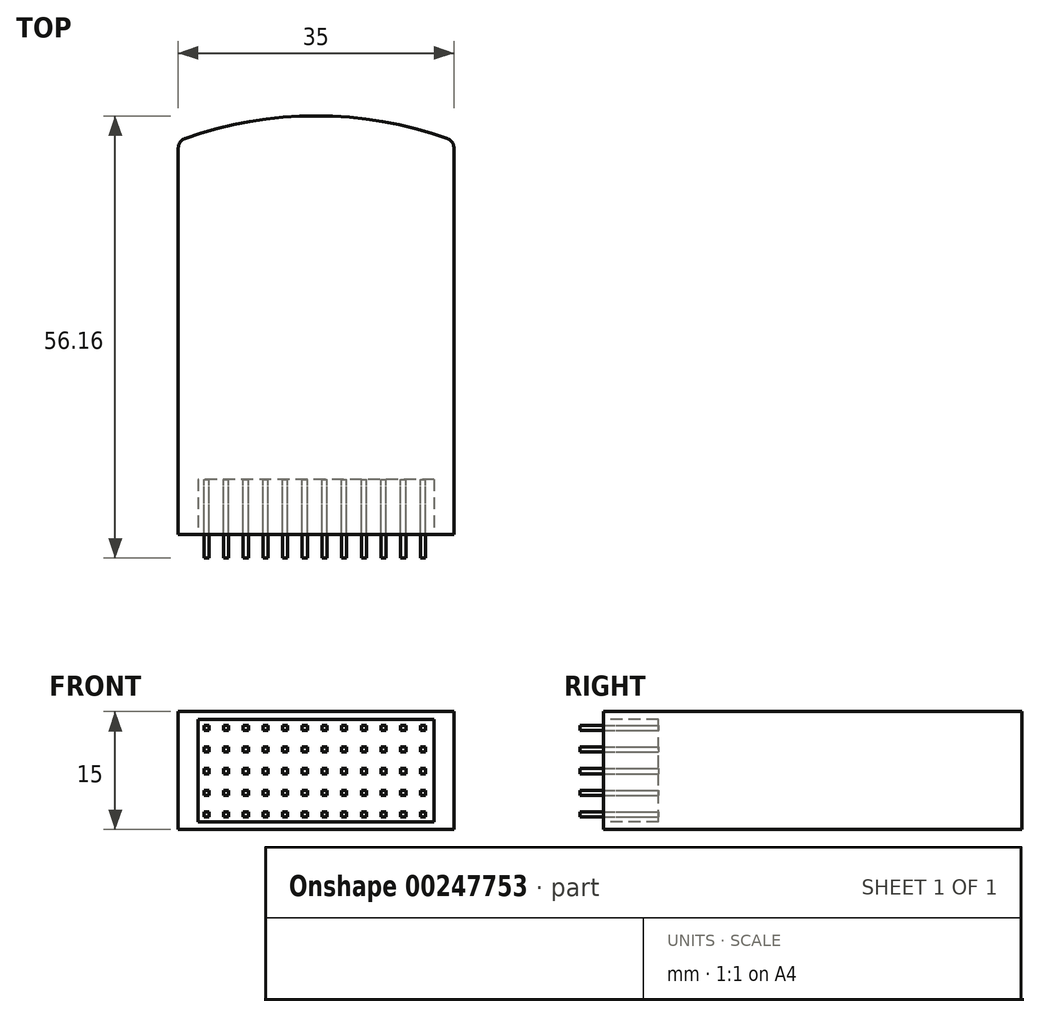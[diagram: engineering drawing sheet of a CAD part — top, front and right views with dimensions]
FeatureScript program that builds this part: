
annotation { "Feature Type Name" : "Feature", "Feature Type Description" : "" }
export const myFeature = defineFeature(function(context is Context, id is Id, definition is map)
    precondition{}
    {
        {
            var Q0;
            Q0=qCreatedBy(makeId("Top.planeOp"),FACE);
            var sketch = newSketch(context, id + "F0", { "sketchPlane" : qUnion([Q0])});
            skLineSegment(sketch, "E0.bottom", {"start": v(17.5, -25) * mm, "end": v(-17.5, -25) * mm});
            skLineSegment(sketch, "E0.top", {"start": v(17.5, 25) * mm, "end": v(-17.5, 25) * mm});
            skLineSegment(sketch, "E0.left", {"start": v(17.5, -25) * mm, "end": v(17.5, 25) * mm});
            skLineSegment(sketch, "E0.right", {"start": v(-17.5, -25) * mm, "end": v(-17.5, 25) * mm});
            skPoint(sketch, "E0.middle", {"position": v(0, 0) * mm});
            skPoint(sketch, "E1.startSnap0", {"position": v(0, 25) * mm});
            skArc(sketch, "E2", {"start": v(17.5, 25) * mm, "mid": v(0, 28.16) * mm, "end": v(-17.5, 25) * mm});
            skSolve(sketch);
        }
        {
            var Q0;
            Q0 = qSketchRegion(id + "F0", true);
            extrude(context, id + "F1", {"entities" : qUnion([Q0]), "depth" : 15 * mm, "symmetric" : true});
        }
        {
            var Q0;
            Q0=makeQuery(id+"F1.opExtrude","SWEPT_EDGE",EDGE,{"disambiguationData":[OSD([sQuery(id+"F0.wireOp",EDGE,"E0.top"),sQuery(id+"F0.wireOp",EDGE,"E0.left"),sQuery(id+"F0.wireOp",EDGE,"yyNhz9fe-Qt3a-qb7e-cI5q-L0wKWxCpfobD")])]});
            var Q1;
            Q1=makeQuery(id+"F1.opExtrude","SWEPT_EDGE",EDGE,{"disambiguationData":[OSD([sQuery(id+"F0.wireOp",EDGE,"E0.top"),sQuery(id+"F0.wireOp",EDGE,"E0.right"),sQuery(id+"F0.wireOp",EDGE,"NXXVwKCm-iX8Y-aLn6-gdMx-Pbhs1YLQSOhg")])]});
            fillet(context, id + "F2", {"entities" : qUnion([Q0, Q1]), "radius" : 1.25 * mm, "tangentPropagation" : true, "allowEdgeOverflow" : false});
        }
        {
            var Q0;
            Q0=makeQuery(id+"F1.opExtrude","SWEPT_FACE",FACE,{"disambiguationData":[OSD([sQuery(id+"F0.wireOp",EDGE,"E0.bottom")])]});
            var sketch = newSketch(context, id + "F3", { "sketchPlane" : qUnion([Q0])});
            skPoint(sketch, "E3.0", {"position": v(0, 0) * mm});
            skLineSegment(sketch, "E4.bottom", {"start": v(15, -6.5) * mm, "end": v(-15, -6.5) * mm});
            skLineSegment(sketch, "E4.top", {"start": v(15, 6.5) * mm, "end": v(-15, 6.5) * mm});
            skLineSegment(sketch, "E4.left", {"start": v(15, -6.5) * mm, "end": v(15, 6.5) * mm});
            skLineSegment(sketch, "E4.right", {"start": v(-15, -6.5) * mm, "end": v(-15, 6.5) * mm});
            skSolve(sketch);
        }
        {
            var Q0;
            Q0 = qSketchRegion(id + "F3", true);
            extrude(context, id + "F4", {"entities" : qUnion([Q0]), "operationType" : NewBodyOperationType.REMOVE, "oppositeDirection" : true, "depth" : 7 * mm});
        }
        {
            var Q0;
            Q0=makeQuery(id+"F4.boolean.opBoolean","COPY",FACE,{"derivedFrom":makeQuery(id+"F4.opExtrude","CAP_FACE",FACE,{"disambiguationData":[OSD([sQuery(id+"F3.wireOp",EDGE,"E4.bottom"),sQuery(id+"F3.wireOp",EDGE,"E4.top"),sQuery(id+"F3.wireOp",EDGE,"E4.left"),sQuery(id+"F3.wireOp",EDGE,"E4.right")])],"isStart":false})});
            var sketch = newSketch(context, id + "F5", { "sketchPlane" : qUnion([Q0])});
            skLineSegment(sketch, "E5.bottom", {"start": v(-14.25, 5.75) * mm, "end": v(-13.6, 5.75) * mm});
            skLineSegment(sketch, "E5.top", {"start": v(-14.25, 5.1) * mm, "end": v(-13.6, 5.1) * mm});
            skLineSegment(sketch, "E5.left", {"start": v(-14.25, 5.75) * mm, "end": v(-14.25, 5.1) * mm});
            skLineSegment(sketch, "E5.right", {"start": v(-13.6, 5.75) * mm, "end": v(-13.6, 5.1) * mm});
            skLineSegment(sketch, "E6.1.0.0", {"start": v(-11.75, 5.75) * mm, "end": v(-11.1, 5.75) * mm});
            skLineSegment(sketch, "E6.1.0.1", {"start": v(-11.75, 5.75) * mm, "end": v(-11.75, 5.1) * mm});
            skLineSegment(sketch, "E6.1.0.2", {"start": v(-11.75, 5.1) * mm, "end": v(-11.1, 5.1) * mm});
            skLineSegment(sketch, "E6.1.0.3", {"start": v(-11.1, 5.75) * mm, "end": v(-11.1, 5.1) * mm});
            skLineSegment(sketch, "E6.2.0.0", {"start": v(-9.25, 5.75) * mm, "end": v(-8.6, 5.75) * mm});
            skLineSegment(sketch, "E6.2.0.1", {"start": v(-9.25, 5.75) * mm, "end": v(-9.25, 5.1) * mm});
            skLineSegment(sketch, "E6.2.0.2", {"start": v(-9.25, 5.1) * mm, "end": v(-8.6, 5.1) * mm});
            skLineSegment(sketch, "E6.2.0.3", {"start": v(-8.6, 5.75) * mm, "end": v(-8.6, 5.1) * mm});
            skLineSegment(sketch, "E6.3.0.0", {"start": v(-6.75, 5.75) * mm, "end": v(-6.1, 5.75) * mm});
            skLineSegment(sketch, "E6.3.0.1", {"start": v(-6.75, 5.75) * mm, "end": v(-6.75, 5.1) * mm});
            skLineSegment(sketch, "E6.3.0.2", {"start": v(-6.75, 5.1) * mm, "end": v(-6.1, 5.1) * mm});
            skLineSegment(sketch, "E6.3.0.3", {"start": v(-6.1, 5.75) * mm, "end": v(-6.1, 5.1) * mm});
            skLineSegment(sketch, "E6.4.0.0", {"start": v(-4.25, 5.75) * mm, "end": v(-3.6, 5.75) * mm});
            skLineSegment(sketch, "E6.4.0.1", {"start": v(-4.25, 5.75) * mm, "end": v(-4.25, 5.1) * mm});
            skLineSegment(sketch, "E6.4.0.2", {"start": v(-4.25, 5.1) * mm, "end": v(-3.6, 5.1) * mm});
            skLineSegment(sketch, "E6.4.0.3", {"start": v(-3.6, 5.75) * mm, "end": v(-3.6, 5.1) * mm});
            skLineSegment(sketch, "E6.5.0.0", {"start": v(-1.75, 5.75) * mm, "end": v(-1.1, 5.75) * mm});
            skLineSegment(sketch, "E6.5.0.1", {"start": v(-1.75, 5.75) * mm, "end": v(-1.75, 5.1) * mm});
            skLineSegment(sketch, "E6.5.0.2", {"start": v(-1.75, 5.1) * mm, "end": v(-1.1, 5.1) * mm});
            skLineSegment(sketch, "E6.5.0.3", {"start": v(-1.1, 5.75) * mm, "end": v(-1.1, 5.1) * mm});
            skLineSegment(sketch, "E6.6.0.0", {"start": v(0.75, 5.75) * mm, "end": v(1.4, 5.75) * mm});
            skLineSegment(sketch, "E6.6.0.1", {"start": v(0.75, 5.75) * mm, "end": v(0.75, 5.1) * mm});
            skLineSegment(sketch, "E6.6.0.2", {"start": v(0.75, 5.1) * mm, "end": v(1.4, 5.1) * mm});
            skLineSegment(sketch, "E6.6.0.3", {"start": v(1.4, 5.75) * mm, "end": v(1.4, 5.1) * mm});
            skLineSegment(sketch, "E6.7.0.0", {"start": v(3.25, 5.75) * mm, "end": v(3.9, 5.75) * mm});
            skLineSegment(sketch, "E6.7.0.1", {"start": v(3.25, 5.75) * mm, "end": v(3.25, 5.1) * mm});
            skLineSegment(sketch, "E6.7.0.2", {"start": v(3.25, 5.1) * mm, "end": v(3.9, 5.1) * mm});
            skLineSegment(sketch, "E6.7.0.3", {"start": v(3.9, 5.75) * mm, "end": v(3.9, 5.1) * mm});
            skLineSegment(sketch, "E6.8.0.0", {"start": v(5.75, 5.75) * mm, "end": v(6.4, 5.75) * mm});
            skLineSegment(sketch, "E6.8.0.1", {"start": v(5.75, 5.75) * mm, "end": v(5.75, 5.1) * mm});
            skLineSegment(sketch, "E6.8.0.2", {"start": v(5.75, 5.1) * mm, "end": v(6.4, 5.1) * mm});
            skLineSegment(sketch, "E6.8.0.3", {"start": v(6.4, 5.75) * mm, "end": v(6.4, 5.1) * mm});
            skLineSegment(sketch, "E6.9.0.0", {"start": v(8.25, 5.75) * mm, "end": v(8.9, 5.75) * mm});
            skLineSegment(sketch, "E6.9.0.1", {"start": v(8.25, 5.75) * mm, "end": v(8.25, 5.1) * mm});
            skLineSegment(sketch, "E6.9.0.2", {"start": v(8.25, 5.1) * mm, "end": v(8.9, 5.1) * mm});
            skLineSegment(sketch, "E6.9.0.3", {"start": v(8.9, 5.75) * mm, "end": v(8.9, 5.1) * mm});
            skLineSegment(sketch, "E6.10.0.0", {"start": v(10.75, 5.75) * mm, "end": v(11.4, 5.75) * mm});
            skLineSegment(sketch, "E6.10.0.1", {"start": v(10.75, 5.75) * mm, "end": v(10.75, 5.1) * mm});
            skLineSegment(sketch, "E6.10.0.2", {"start": v(10.75, 5.1) * mm, "end": v(11.4, 5.1) * mm});
            skLineSegment(sketch, "E6.10.0.3", {"start": v(11.4, 5.75) * mm, "end": v(11.4, 5.1) * mm});
            skLineSegment(sketch, "E6.direction1", {"start": v(-14.25, 5.75) * mm, "end": v(-11.75, 5.75) * mm, "construction": true});
            skLineSegment(sketch, "E7.0.11.0", {"start": v(13.25, 5.75) * mm, "end": v(13.9, 5.75) * mm});
            skLineSegment(sketch, "E7.3.11.0", {"start": v(13.25, 5.75) * mm, "end": v(13.25, 5.1) * mm});
            skLineSegment(sketch, "E7.6.11.0", {"start": v(13.25, 5.1) * mm, "end": v(13.9, 5.1) * mm});
            skLineSegment(sketch, "E7.9.11.0", {"start": v(13.9, 5.75) * mm, "end": v(13.9, 5.1) * mm});
            skLineSegment(sketch, "E8.1.0.0", {"start": v(0.75, 3) * mm, "end": v(0.75, 2.35) * mm});
            skLineSegment(sketch, "E8.1.0.1", {"start": v(-6.75, 3) * mm, "end": v(-6.1, 3) * mm});
            skLineSegment(sketch, "E8.1.0.2", {"start": v(10.75, 3) * mm, "end": v(10.75, 2.35) * mm});
            skLineSegment(sketch, "E8.1.0.3", {"start": v(5.75, 2.35) * mm, "end": v(6.4, 2.35) * mm});
            skLineSegment(sketch, "E8.1.0.4", {"start": v(-4.25, 2.35) * mm, "end": v(-3.6, 2.35) * mm});
            skLineSegment(sketch, "E8.1.0.5", {"start": v(3.9, 3) * mm, "end": v(3.9, 2.35) * mm});
            skLineSegment(sketch, "E8.1.0.6", {"start": v(8.25, 2.35) * mm, "end": v(8.9, 2.35) * mm});
            skLineSegment(sketch, "E8.1.0.7", {"start": v(13.25, 2.35) * mm, "end": v(13.9, 2.35) * mm});
            skLineSegment(sketch, "E8.1.0.8", {"start": v(-1.75, 2.35) * mm, "end": v(-1.1, 2.35) * mm});
            skLineSegment(sketch, "E8.1.0.9", {"start": v(-8.6, 3) * mm, "end": v(-8.6, 2.35) * mm});
            skLineSegment(sketch, "E8.1.0.10", {"start": v(-9.25, 2.35) * mm, "end": v(-8.6, 2.35) * mm});
            skLineSegment(sketch, "E8.1.0.11", {"start": v(-9.25, 3) * mm, "end": v(-9.25, 2.35) * mm});
            skLineSegment(sketch, "E8.1.0.12", {"start": v(-9.25, 3) * mm, "end": v(-8.6, 3) * mm});
            skLineSegment(sketch, "E8.1.0.13", {"start": v(-11.1, 3) * mm, "end": v(-11.1, 2.35) * mm});
            skLineSegment(sketch, "E8.1.0.14", {"start": v(-11.75, 2.35) * mm, "end": v(-11.1, 2.35) * mm});
            skLineSegment(sketch, "E8.1.0.15", {"start": v(-11.75, 3) * mm, "end": v(-11.75, 2.35) * mm});
            skLineSegment(sketch, "E8.1.0.16", {"start": v(-11.75, 3) * mm, "end": v(-11.1, 3) * mm});
            skLineSegment(sketch, "E8.1.0.17", {"start": v(-13.6, 3) * mm, "end": v(-13.6, 2.35) * mm});
            skLineSegment(sketch, "E8.1.0.18", {"start": v(-14.25, 3) * mm, "end": v(-14.25, 2.35) * mm});
            skLineSegment(sketch, "E8.1.0.19", {"start": v(-14.25, 2.35) * mm, "end": v(-13.6, 2.35) * mm});
            skLineSegment(sketch, "E8.1.0.20", {"start": v(-4.25, 3) * mm, "end": v(-4.25, 2.35) * mm});
            skLineSegment(sketch, "E8.1.0.21", {"start": v(-6.1, 3) * mm, "end": v(-6.1, 2.35) * mm});
            skLineSegment(sketch, "E8.1.0.22", {"start": v(8.25, 3) * mm, "end": v(8.25, 2.35) * mm});
            skLineSegment(sketch, "E8.1.0.23", {"start": v(3.25, 2.35) * mm, "end": v(3.9, 2.35) * mm});
            skLineSegment(sketch, "E8.1.0.24", {"start": v(13.25, 3) * mm, "end": v(13.25, 2.35) * mm});
            skLineSegment(sketch, "E8.1.0.25", {"start": v(-6.75, 2.35) * mm, "end": v(-6.1, 2.35) * mm});
            skLineSegment(sketch, "E8.1.0.26", {"start": v(-1.75, 3) * mm, "end": v(-1.75, 2.35) * mm});
            skLineSegment(sketch, "E8.1.0.27", {"start": v(-6.75, 3) * mm, "end": v(-6.75, 2.35) * mm});
            skLineSegment(sketch, "E8.1.0.28", {"start": v(0.75, 3) * mm, "end": v(1.4, 3) * mm});
            skLineSegment(sketch, "E8.1.0.29", {"start": v(10.75, 3) * mm, "end": v(11.4, 3) * mm});
            skLineSegment(sketch, "E8.1.0.30", {"start": v(3.25, 3) * mm, "end": v(3.9, 3) * mm});
            skLineSegment(sketch, "E8.1.0.31", {"start": v(-14.25, 3) * mm, "end": v(-11.75, 3) * mm, "construction": true});
            skLineSegment(sketch, "E8.1.0.32", {"start": v(5.75, 3) * mm, "end": v(5.75, 2.35) * mm});
            skLineSegment(sketch, "E8.1.0.33", {"start": v(-1.1, 3) * mm, "end": v(-1.1, 2.35) * mm});
            skLineSegment(sketch, "E8.1.0.34", {"start": v(8.9, 3) * mm, "end": v(8.9, 2.35) * mm});
            skLineSegment(sketch, "E8.1.0.35", {"start": v(8.25, 3) * mm, "end": v(8.9, 3) * mm});
            skLineSegment(sketch, "E8.1.0.36", {"start": v(3.25, 3) * mm, "end": v(3.25, 2.35) * mm});
            skLineSegment(sketch, "E8.1.0.37", {"start": v(13.25, 3) * mm, "end": v(13.9, 3) * mm});
            skLineSegment(sketch, "E8.1.0.38", {"start": v(-1.75, 3) * mm, "end": v(-1.1, 3) * mm});
            skLineSegment(sketch, "E8.1.0.39", {"start": v(1.4, 3) * mm, "end": v(1.4, 2.35) * mm});
            skLineSegment(sketch, "E8.1.0.40", {"start": v(11.4, 3) * mm, "end": v(11.4, 2.35) * mm});
            skLineSegment(sketch, "E8.1.0.41", {"start": v(5.75, 3) * mm, "end": v(6.4, 3) * mm});
            skLineSegment(sketch, "E8.1.0.42", {"start": v(13.9, 3) * mm, "end": v(13.9, 2.35) * mm});
            skLineSegment(sketch, "E8.1.0.43", {"start": v(-4.25, 3) * mm, "end": v(-3.6, 3) * mm});
            skLineSegment(sketch, "E8.1.0.44", {"start": v(6.4, 3) * mm, "end": v(6.4, 2.35) * mm});
            skLineSegment(sketch, "E8.1.0.45", {"start": v(-3.6, 3) * mm, "end": v(-3.6, 2.35) * mm});
            skLineSegment(sketch, "E8.1.0.46", {"start": v(0.75, 2.35) * mm, "end": v(1.4, 2.35) * mm});
            skLineSegment(sketch, "E8.1.0.47", {"start": v(10.75, 2.35) * mm, "end": v(11.4, 2.35) * mm});
            skLineSegment(sketch, "E8.1.0.48", {"start": v(-14.25, 3) * mm, "end": v(-13.6, 3) * mm});
            skLineSegment(sketch, "E8.2.0.0", {"start": v(0.75, 0.25) * mm, "end": v(0.75, -0.4) * mm});
            skLineSegment(sketch, "E8.2.0.1", {"start": v(-6.75, 0.25) * mm, "end": v(-6.1, 0.25) * mm});
            skLineSegment(sketch, "E8.2.0.2", {"start": v(10.75, 0.25) * mm, "end": v(10.75, -0.4) * mm});
            skLineSegment(sketch, "E8.2.0.3", {"start": v(5.75, -0.4) * mm, "end": v(6.4, -0.4) * mm});
            skLineSegment(sketch, "E8.2.0.4", {"start": v(-4.25, -0.4) * mm, "end": v(-3.6, -0.4) * mm});
            skLineSegment(sketch, "E8.2.0.5", {"start": v(3.9, 0.25) * mm, "end": v(3.9, -0.4) * mm});
            skLineSegment(sketch, "E8.2.0.6", {"start": v(8.25, -0.4) * mm, "end": v(8.9, -0.4) * mm});
            skLineSegment(sketch, "E8.2.0.7", {"start": v(13.25, -0.4) * mm, "end": v(13.9, -0.4) * mm});
            skLineSegment(sketch, "E8.2.0.8", {"start": v(-1.75, -0.4) * mm, "end": v(-1.1, -0.4) * mm});
            skLineSegment(sketch, "E8.2.0.9", {"start": v(-8.6, 0.25) * mm, "end": v(-8.6, -0.4) * mm});
            skLineSegment(sketch, "E8.2.0.10", {"start": v(-9.25, -0.4) * mm, "end": v(-8.6, -0.4) * mm});
            skLineSegment(sketch, "E8.2.0.11", {"start": v(-9.25, 0.25) * mm, "end": v(-9.25, -0.4) * mm});
            skLineSegment(sketch, "E8.2.0.12", {"start": v(-9.25, 0.25) * mm, "end": v(-8.6, 0.25) * mm});
            skLineSegment(sketch, "E8.2.0.13", {"start": v(-11.1, 0.25) * mm, "end": v(-11.1, -0.4) * mm});
            skLineSegment(sketch, "E8.2.0.14", {"start": v(-11.75, -0.4) * mm, "end": v(-11.1, -0.4) * mm});
            skLineSegment(sketch, "E8.2.0.15", {"start": v(-11.75, 0.25) * mm, "end": v(-11.75, -0.4) * mm});
            skLineSegment(sketch, "E8.2.0.16", {"start": v(-11.75, 0.25) * mm, "end": v(-11.1, 0.25) * mm});
            skLineSegment(sketch, "E8.2.0.17", {"start": v(-13.6, 0.25) * mm, "end": v(-13.6, -0.4) * mm});
            skLineSegment(sketch, "E8.2.0.18", {"start": v(-14.25, 0.25) * mm, "end": v(-14.25, -0.4) * mm});
            skLineSegment(sketch, "E8.2.0.19", {"start": v(-14.25, -0.4) * mm, "end": v(-13.6, -0.4) * mm});
            skLineSegment(sketch, "E8.2.0.20", {"start": v(-4.25, 0.25) * mm, "end": v(-4.25, -0.4) * mm});
            skLineSegment(sketch, "E8.2.0.21", {"start": v(-6.1, 0.25) * mm, "end": v(-6.1, -0.4) * mm});
            skLineSegment(sketch, "E8.2.0.22", {"start": v(8.25, 0.25) * mm, "end": v(8.25, -0.4) * mm});
            skLineSegment(sketch, "E8.2.0.23", {"start": v(3.25, -0.4) * mm, "end": v(3.9, -0.4) * mm});
            skLineSegment(sketch, "E8.2.0.24", {"start": v(13.25, 0.25) * mm, "end": v(13.25, -0.4) * mm});
            skLineSegment(sketch, "E8.2.0.25", {"start": v(-6.75, -0.4) * mm, "end": v(-6.1, -0.4) * mm});
            skLineSegment(sketch, "E8.2.0.26", {"start": v(-1.75, 0.25) * mm, "end": v(-1.75, -0.4) * mm});
            skLineSegment(sketch, "E8.2.0.27", {"start": v(-6.75, 0.25) * mm, "end": v(-6.75, -0.4) * mm});
            skLineSegment(sketch, "E8.2.0.28", {"start": v(0.75, 0.25) * mm, "end": v(1.4, 0.25) * mm});
            skLineSegment(sketch, "E8.2.0.29", {"start": v(10.75, 0.25) * mm, "end": v(11.4, 0.25) * mm});
            skLineSegment(sketch, "E8.2.0.30", {"start": v(3.25, 0.25) * mm, "end": v(3.9, 0.25) * mm});
            skLineSegment(sketch, "E8.2.0.31", {"start": v(-14.25, 0.25) * mm, "end": v(-11.75, 0.25) * mm, "construction": true});
            skLineSegment(sketch, "E8.2.0.32", {"start": v(5.75, 0.25) * mm, "end": v(5.75, -0.4) * mm});
            skLineSegment(sketch, "E8.2.0.33", {"start": v(-1.1, 0.25) * mm, "end": v(-1.1, -0.4) * mm});
            skLineSegment(sketch, "E8.2.0.34", {"start": v(8.9, 0.25) * mm, "end": v(8.9, -0.4) * mm});
            skLineSegment(sketch, "E8.2.0.35", {"start": v(8.25, 0.25) * mm, "end": v(8.9, 0.25) * mm});
            skLineSegment(sketch, "E8.2.0.36", {"start": v(3.25, 0.25) * mm, "end": v(3.25, -0.4) * mm});
            skLineSegment(sketch, "E8.2.0.37", {"start": v(13.25, 0.25) * mm, "end": v(13.9, 0.25) * mm});
            skLineSegment(sketch, "E8.2.0.38", {"start": v(-1.75, 0.25) * mm, "end": v(-1.1, 0.25) * mm});
            skLineSegment(sketch, "E8.2.0.39", {"start": v(1.4, 0.25) * mm, "end": v(1.4, -0.4) * mm});
            skLineSegment(sketch, "E8.2.0.40", {"start": v(11.4, 0.25) * mm, "end": v(11.4, -0.4) * mm});
            skLineSegment(sketch, "E8.2.0.41", {"start": v(5.75, 0.25) * mm, "end": v(6.4, 0.25) * mm});
            skLineSegment(sketch, "E8.2.0.42", {"start": v(13.9, 0.25) * mm, "end": v(13.9, -0.4) * mm});
            skLineSegment(sketch, "E8.2.0.43", {"start": v(-4.25, 0.25) * mm, "end": v(-3.6, 0.25) * mm});
            skLineSegment(sketch, "E8.2.0.44", {"start": v(6.4, 0.25) * mm, "end": v(6.4, -0.4) * mm});
            skLineSegment(sketch, "E8.2.0.45", {"start": v(-3.6, 0.25) * mm, "end": v(-3.6, -0.4) * mm});
            skLineSegment(sketch, "E8.2.0.46", {"start": v(0.75, -0.4) * mm, "end": v(1.4, -0.4) * mm});
            skLineSegment(sketch, "E8.2.0.47", {"start": v(10.75, -0.4) * mm, "end": v(11.4, -0.4) * mm});
            skLineSegment(sketch, "E8.2.0.48", {"start": v(-14.25, 0.25) * mm, "end": v(-13.6, 0.25) * mm});
            skLineSegment(sketch, "E8.3.0.0", {"start": v(0.75, -2.5) * mm, "end": v(0.75, -3.15) * mm});
            skLineSegment(sketch, "E8.3.0.1", {"start": v(-6.75, -2.5) * mm, "end": v(-6.1, -2.5) * mm});
            skLineSegment(sketch, "E8.3.0.2", {"start": v(10.75, -2.5) * mm, "end": v(10.75, -3.15) * mm});
            skLineSegment(sketch, "E8.3.0.3", {"start": v(5.75, -3.15) * mm, "end": v(6.4, -3.15) * mm});
            skLineSegment(sketch, "E8.3.0.4", {"start": v(-4.25, -3.15) * mm, "end": v(-3.6, -3.15) * mm});
            skLineSegment(sketch, "E8.3.0.5", {"start": v(3.9, -2.5) * mm, "end": v(3.9, -3.15) * mm});
            skLineSegment(sketch, "E8.3.0.6", {"start": v(8.25, -3.15) * mm, "end": v(8.9, -3.15) * mm});
            skLineSegment(sketch, "E8.3.0.7", {"start": v(13.25, -3.15) * mm, "end": v(13.9, -3.15) * mm});
            skLineSegment(sketch, "E8.3.0.8", {"start": v(-1.75, -3.15) * mm, "end": v(-1.1, -3.15) * mm});
            skLineSegment(sketch, "E8.3.0.9", {"start": v(-8.6, -2.5) * mm, "end": v(-8.6, -3.15) * mm});
            skLineSegment(sketch, "E8.3.0.10", {"start": v(-9.25, -3.15) * mm, "end": v(-8.6, -3.15) * mm});
            skLineSegment(sketch, "E8.3.0.11", {"start": v(-9.25, -2.5) * mm, "end": v(-9.25, -3.15) * mm});
            skLineSegment(sketch, "E8.3.0.12", {"start": v(-9.25, -2.5) * mm, "end": v(-8.6, -2.5) * mm});
            skLineSegment(sketch, "E8.3.0.13", {"start": v(-11.1, -2.5) * mm, "end": v(-11.1, -3.15) * mm});
            skLineSegment(sketch, "E8.3.0.14", {"start": v(-11.75, -3.15) * mm, "end": v(-11.1, -3.15) * mm});
            skLineSegment(sketch, "E8.3.0.15", {"start": v(-11.75, -2.5) * mm, "end": v(-11.75, -3.15) * mm});
            skLineSegment(sketch, "E8.3.0.16", {"start": v(-11.75, -2.5) * mm, "end": v(-11.1, -2.5) * mm});
            skLineSegment(sketch, "E8.3.0.17", {"start": v(-13.6, -2.5) * mm, "end": v(-13.6, -3.15) * mm});
            skLineSegment(sketch, "E8.3.0.18", {"start": v(-14.25, -2.5) * mm, "end": v(-14.25, -3.15) * mm});
            skLineSegment(sketch, "E8.3.0.19", {"start": v(-14.25, -3.15) * mm, "end": v(-13.6, -3.15) * mm});
            skLineSegment(sketch, "E8.3.0.20", {"start": v(-4.25, -2.5) * mm, "end": v(-4.25, -3.15) * mm});
            skLineSegment(sketch, "E8.3.0.21", {"start": v(-6.1, -2.5) * mm, "end": v(-6.1, -3.15) * mm});
            skLineSegment(sketch, "E8.3.0.22", {"start": v(8.25, -2.5) * mm, "end": v(8.25, -3.15) * mm});
            skLineSegment(sketch, "E8.3.0.23", {"start": v(3.25, -3.15) * mm, "end": v(3.9, -3.15) * mm});
            skLineSegment(sketch, "E8.3.0.24", {"start": v(13.25, -2.5) * mm, "end": v(13.25, -3.15) * mm});
            skLineSegment(sketch, "E8.3.0.25", {"start": v(-6.75, -3.15) * mm, "end": v(-6.1, -3.15) * mm});
            skLineSegment(sketch, "E8.3.0.26", {"start": v(-1.75, -2.5) * mm, "end": v(-1.75, -3.15) * mm});
            skLineSegment(sketch, "E8.3.0.27", {"start": v(-6.75, -2.5) * mm, "end": v(-6.75, -3.15) * mm});
            skLineSegment(sketch, "E8.3.0.28", {"start": v(0.75, -2.5) * mm, "end": v(1.4, -2.5) * mm});
            skLineSegment(sketch, "E8.3.0.29", {"start": v(10.75, -2.5) * mm, "end": v(11.4, -2.5) * mm});
            skLineSegment(sketch, "E8.3.0.30", {"start": v(3.25, -2.5) * mm, "end": v(3.9, -2.5) * mm});
            skLineSegment(sketch, "E8.3.0.31", {"start": v(-14.25, -2.5) * mm, "end": v(-11.75, -2.5) * mm, "construction": true});
            skLineSegment(sketch, "E8.3.0.32", {"start": v(5.75, -2.5) * mm, "end": v(5.75, -3.15) * mm});
            skLineSegment(sketch, "E8.3.0.33", {"start": v(-1.1, -2.5) * mm, "end": v(-1.1, -3.15) * mm});
            skLineSegment(sketch, "E8.3.0.34", {"start": v(8.9, -2.5) * mm, "end": v(8.9, -3.15) * mm});
            skLineSegment(sketch, "E8.3.0.35", {"start": v(8.25, -2.5) * mm, "end": v(8.9, -2.5) * mm});
            skLineSegment(sketch, "E8.3.0.36", {"start": v(3.25, -2.5) * mm, "end": v(3.25, -3.15) * mm});
            skLineSegment(sketch, "E8.3.0.37", {"start": v(13.25, -2.5) * mm, "end": v(13.9, -2.5) * mm});
            skLineSegment(sketch, "E8.3.0.38", {"start": v(-1.75, -2.5) * mm, "end": v(-1.1, -2.5) * mm});
            skLineSegment(sketch, "E8.3.0.39", {"start": v(1.4, -2.5) * mm, "end": v(1.4, -3.15) * mm});
            skLineSegment(sketch, "E8.3.0.40", {"start": v(11.4, -2.5) * mm, "end": v(11.4, -3.15) * mm});
            skLineSegment(sketch, "E8.3.0.41", {"start": v(5.75, -2.5) * mm, "end": v(6.4, -2.5) * mm});
            skLineSegment(sketch, "E8.3.0.42", {"start": v(13.9, -2.5) * mm, "end": v(13.9, -3.15) * mm});
            skLineSegment(sketch, "E8.3.0.43", {"start": v(-4.25, -2.5) * mm, "end": v(-3.6, -2.5) * mm});
            skLineSegment(sketch, "E8.3.0.44", {"start": v(6.4, -2.5) * mm, "end": v(6.4, -3.15) * mm});
            skLineSegment(sketch, "E8.3.0.45", {"start": v(-3.6, -2.5) * mm, "end": v(-3.6, -3.15) * mm});
            skLineSegment(sketch, "E8.3.0.46", {"start": v(0.75, -3.15) * mm, "end": v(1.4, -3.15) * mm});
            skLineSegment(sketch, "E8.3.0.47", {"start": v(10.75, -3.15) * mm, "end": v(11.4, -3.15) * mm});
            skLineSegment(sketch, "E8.3.0.48", {"start": v(-14.25, -2.5) * mm, "end": v(-13.6, -2.5) * mm});
            skLineSegment(sketch, "E8.4.0.0", {"start": v(0.75, -5.25) * mm, "end": v(0.75, -5.9) * mm});
            skLineSegment(sketch, "E8.4.0.1", {"start": v(-6.75, -5.25) * mm, "end": v(-6.1, -5.25) * mm});
            skLineSegment(sketch, "E8.4.0.2", {"start": v(10.75, -5.25) * mm, "end": v(10.75, -5.9) * mm});
            skLineSegment(sketch, "E8.4.0.3", {"start": v(5.75, -5.9) * mm, "end": v(6.4, -5.9) * mm});
            skLineSegment(sketch, "E8.4.0.4", {"start": v(-4.25, -5.9) * mm, "end": v(-3.6, -5.9) * mm});
            skLineSegment(sketch, "E8.4.0.5", {"start": v(3.9, -5.25) * mm, "end": v(3.9, -5.9) * mm});
            skLineSegment(sketch, "E8.4.0.6", {"start": v(8.25, -5.9) * mm, "end": v(8.9, -5.9) * mm});
            skLineSegment(sketch, "E8.4.0.7", {"start": v(13.25, -5.9) * mm, "end": v(13.9, -5.9) * mm});
            skLineSegment(sketch, "E8.4.0.8", {"start": v(-1.75, -5.9) * mm, "end": v(-1.1, -5.9) * mm});
            skLineSegment(sketch, "E8.4.0.9", {"start": v(-8.6, -5.25) * mm, "end": v(-8.6, -5.9) * mm});
            skLineSegment(sketch, "E8.4.0.10", {"start": v(-9.25, -5.9) * mm, "end": v(-8.6, -5.9) * mm});
            skLineSegment(sketch, "E8.4.0.11", {"start": v(-9.25, -5.25) * mm, "end": v(-9.25, -5.9) * mm});
            skLineSegment(sketch, "E8.4.0.12", {"start": v(-9.25, -5.25) * mm, "end": v(-8.6, -5.25) * mm});
            skLineSegment(sketch, "E8.4.0.13", {"start": v(-11.1, -5.25) * mm, "end": v(-11.1, -5.9) * mm});
            skLineSegment(sketch, "E8.4.0.14", {"start": v(-11.75, -5.9) * mm, "end": v(-11.1, -5.9) * mm});
            skLineSegment(sketch, "E8.4.0.15", {"start": v(-11.75, -5.25) * mm, "end": v(-11.75, -5.9) * mm});
            skLineSegment(sketch, "E8.4.0.16", {"start": v(-11.75, -5.25) * mm, "end": v(-11.1, -5.25) * mm});
            skLineSegment(sketch, "E8.4.0.17", {"start": v(-13.6, -5.25) * mm, "end": v(-13.6, -5.9) * mm});
            skLineSegment(sketch, "E8.4.0.18", {"start": v(-14.25, -5.25) * mm, "end": v(-14.25, -5.9) * mm});
            skLineSegment(sketch, "E8.4.0.19", {"start": v(-14.25, -5.9) * mm, "end": v(-13.6, -5.9) * mm});
            skLineSegment(sketch, "E8.4.0.20", {"start": v(-4.25, -5.25) * mm, "end": v(-4.25, -5.9) * mm});
            skLineSegment(sketch, "E8.4.0.21", {"start": v(-6.1, -5.25) * mm, "end": v(-6.1, -5.9) * mm});
            skLineSegment(sketch, "E8.4.0.22", {"start": v(8.25, -5.25) * mm, "end": v(8.25, -5.9) * mm});
            skLineSegment(sketch, "E8.4.0.23", {"start": v(3.25, -5.9) * mm, "end": v(3.9, -5.9) * mm});
            skLineSegment(sketch, "E8.4.0.24", {"start": v(13.25, -5.25) * mm, "end": v(13.25, -5.9) * mm});
            skLineSegment(sketch, "E8.4.0.25", {"start": v(-6.75, -5.9) * mm, "end": v(-6.1, -5.9) * mm});
            skLineSegment(sketch, "E8.4.0.26", {"start": v(-1.75, -5.25) * mm, "end": v(-1.75, -5.9) * mm});
            skLineSegment(sketch, "E8.4.0.27", {"start": v(-6.75, -5.25) * mm, "end": v(-6.75, -5.9) * mm});
            skLineSegment(sketch, "E8.4.0.28", {"start": v(0.75, -5.25) * mm, "end": v(1.4, -5.25) * mm});
            skLineSegment(sketch, "E8.4.0.29", {"start": v(10.75, -5.25) * mm, "end": v(11.4, -5.25) * mm});
            skLineSegment(sketch, "E8.4.0.30", {"start": v(3.25, -5.25) * mm, "end": v(3.9, -5.25) * mm});
            skLineSegment(sketch, "E8.4.0.31", {"start": v(-14.25, -5.25) * mm, "end": v(-11.75, -5.25) * mm, "construction": true});
            skLineSegment(sketch, "E8.4.0.32", {"start": v(5.75, -5.25) * mm, "end": v(5.75, -5.9) * mm});
            skLineSegment(sketch, "E8.4.0.33", {"start": v(-1.1, -5.25) * mm, "end": v(-1.1, -5.9) * mm});
            skLineSegment(sketch, "E8.4.0.34", {"start": v(8.9, -5.25) * mm, "end": v(8.9, -5.9) * mm});
            skLineSegment(sketch, "E8.4.0.35", {"start": v(8.25, -5.25) * mm, "end": v(8.9, -5.25) * mm});
            skLineSegment(sketch, "E8.4.0.36", {"start": v(3.25, -5.25) * mm, "end": v(3.25, -5.9) * mm});
            skLineSegment(sketch, "E8.4.0.37", {"start": v(13.25, -5.25) * mm, "end": v(13.9, -5.25) * mm});
            skLineSegment(sketch, "E8.4.0.38", {"start": v(-1.75, -5.25) * mm, "end": v(-1.1, -5.25) * mm});
            skLineSegment(sketch, "E8.4.0.39", {"start": v(1.4, -5.25) * mm, "end": v(1.4, -5.9) * mm});
            skLineSegment(sketch, "E8.4.0.40", {"start": v(11.4, -5.25) * mm, "end": v(11.4, -5.9) * mm});
            skLineSegment(sketch, "E8.4.0.41", {"start": v(5.75, -5.25) * mm, "end": v(6.4, -5.25) * mm});
            skLineSegment(sketch, "E8.4.0.42", {"start": v(13.9, -5.25) * mm, "end": v(13.9, -5.9) * mm});
            skLineSegment(sketch, "E8.4.0.43", {"start": v(-4.25, -5.25) * mm, "end": v(-3.6, -5.25) * mm});
            skLineSegment(sketch, "E8.4.0.44", {"start": v(6.4, -5.25) * mm, "end": v(6.4, -5.9) * mm});
            skLineSegment(sketch, "E8.4.0.45", {"start": v(-3.6, -5.25) * mm, "end": v(-3.6, -5.9) * mm});
            skLineSegment(sketch, "E8.4.0.46", {"start": v(0.75, -5.9) * mm, "end": v(1.4, -5.9) * mm});
            skLineSegment(sketch, "E8.4.0.47", {"start": v(10.75, -5.9) * mm, "end": v(11.4, -5.9) * mm});
            skLineSegment(sketch, "E8.4.0.48", {"start": v(-14.25, -5.25) * mm, "end": v(-13.6, -5.25) * mm});
            skLineSegment(sketch, "E8.direction1", {"start": v(-14.25, 5.1) * mm, "end": v(-14.25, 2.35) * mm, "construction": true});
            skSolve(sketch);
        }
        {
            var Q0;
            Q0 = qSketchRegion(id + "F5", true);
            extrude(context, id + "F6", {"entities" : qUnion([Q0]), "operationType" : NewBodyOperationType.ADD, "depth" : 10 * mm});
        }
    });
